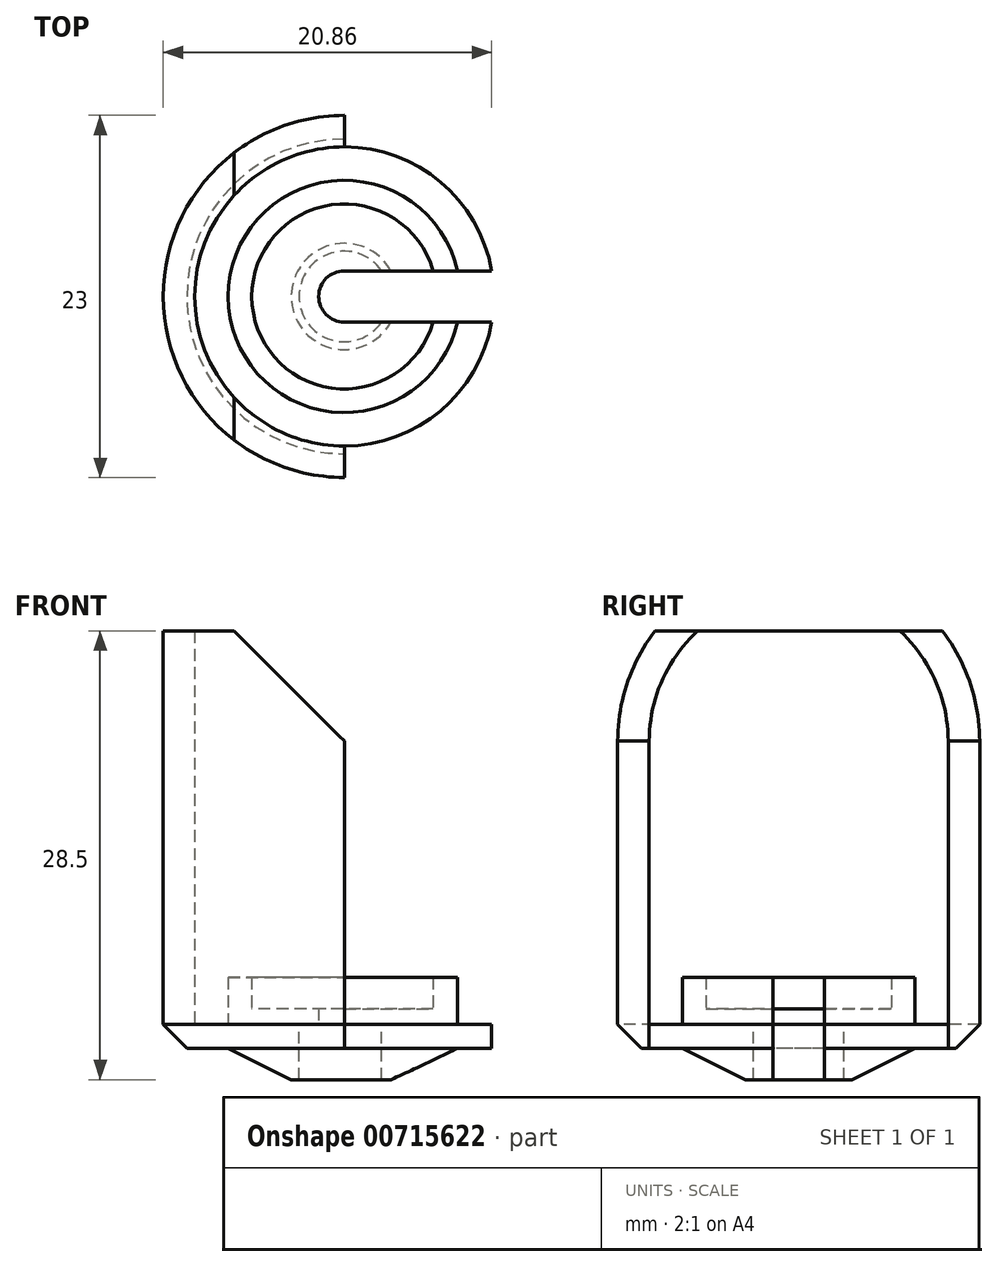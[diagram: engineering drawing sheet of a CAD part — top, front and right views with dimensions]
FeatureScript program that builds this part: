
annotation { "Feature Type Name" : "Feature", "Feature Type Description" : "" }
export const myFeature = defineFeature(function(context is Context, id is Id, definition is map)
    precondition{}
    {
        {
            var Q0;
            Q0=qCreatedBy(makeId("Top.planeOp"),FACE);
            var sketch = newSketch(context, id + "F0", { "sketchPlane" : qUnion([Q0])});
            skArc(sketch, "E0", {"start": v(9.36, 1.63) * mm, "mid": v(-9.5, 0) * mm, "end": v(9.36, -1.62) * mm});
            skArc(sketch, "E1", {"start": v(7.2, 1.62) * mm, "mid": v(-7.38, 0) * mm, "end": v(7.2, -1.63) * mm});
            skArc(sketch, "E2.0", {"start": v(5.65, 1.62) * mm, "mid": v(-5.88, 0) * mm, "end": v(5.65, -1.63) * mm});
            skArc(sketch, "E3", {"start": v(2.37, 1.63) * mm, "mid": v(-2.88, 0) * mm, "end": v(2.37, -1.62) * mm});
            skArc(sketch, "E4", {"start": v(0, 1.63) * mm, "mid": v(-1.63, 0) * mm, "end": v(0, -1.63) * mm});
            skLineSegment(sketch, "E5", {"start": v(0, 1.63) * mm, "end": v(9.36, 1.63) * mm});
            skLineSegment(sketch, "E6", {"start": v(0, -1.63) * mm, "end": v(9.36, -1.63) * mm});
            skArc(sketch, "E7.0", {"start": v(0, 11.5) * mm, "mid": v(-11.5, 0) * mm, "end": v(0, -11.5) * mm});
            skLineSegment(sketch, "E8", {"start": v(0, 9.5) * mm, "end": v(0, 11.5) * mm});
            skLineSegment(sketch, "E9", {"start": v(0, -9.5) * mm, "end": v(0, -11.5) * mm});
            skSolve(sketch);
        }
        {
            var Q0;
            {var subQ0=sQuery(id+"F0.wireOp",EDGE,"E1");Q0=makeQuery(id+"F0.imprint","IMPRINT",FACE,{"disambiguationData":[TD([[makeQuery(id+"F0.imprint","IMPRINT",EDGE,{"derivedFrom":subQ0}),1.0]])]});}
            extrude(context, id + "F1", {"entities" : qUnion([Q0]), "depth" : 3 * mm, "offsetDistance" : 25 * mm});
        }
        {
            var Q0;
            {var subQ0=sQuery(id+"F0.wireOp",EDGE,"E2.0");Q0=makeQuery(id+"F0.imprint","IMPRINT",FACE,{"disambiguationData":[TD([[makeQuery(id+"F0.imprint","IMPRINT",EDGE,{"derivedFrom":subQ0}),1.0]])]});}
            var Q1;
            {var subQ0=sQuery(id+"F0.wireOp",EDGE,"E3");Q1=makeQuery(id+"F0.imprint","IMPRINT",FACE,{"disambiguationData":[TD([[makeQuery(id+"F0.imprint","IMPRINT",EDGE,{"derivedFrom":subQ0}),1.0]])]});}
            extrude(context, id + "F2", {"entities" : qUnion([Q0, Q1]), "operationType" : NewBodyOperationType.ADD, "depth" : 1 * mm, "offsetDistance" : 25 * mm});
        }
        {
            var Q0;
            {var subQ0=sQuery(id+"F0.wireOp",EDGE,"E1");Q0=makeQuery(id+"F0.imprint","IMPRINT",FACE,{"disambiguationData":[TD([[makeQuery(id+"F0.imprint","IMPRINT",EDGE,{"derivedFrom":subQ0}),1.0]])]});}
            var Q1;
            {var subQ0=sQuery(id+"F0.wireOp",EDGE,"E2.0");Q1=makeQuery(id+"F0.imprint","IMPRINT",FACE,{"disambiguationData":[TD([[makeQuery(id+"F0.imprint","IMPRINT",EDGE,{"derivedFrom":subQ0}),1.0]])]});}
            extrude(context, id + "F3", {"entities" : qUnion([Q0, Q1]), "operationType" : NewBodyOperationType.ADD, "oppositeDirection" : true, "depth" : 3.5 * mm, "offsetDistance" : 25 * mm});
        }
        {
            var Q0;
            {var subQ0=sQuery(id+"F0.wireOp",EDGE,"E1");Q0=makeQuery(id+"F0.imprint","IMPRINT",FACE,{"disambiguationData":[TD([[makeQuery(id+"F0.imprint","IMPRINT",EDGE,{"derivedFrom":subQ0}),-1.0]])]});}
            extrude(context, id + "F4", {"entities" : qUnion([Q0]), "operationType" : NewBodyOperationType.ADD, "oppositeDirection" : true, "depth" : 1.5 * mm, "offsetDistance" : 25 * mm});
        }
        {
            var Q0;
            Q0=makeQuery(id+"F0.imprint","IMPRINT",FACE,{"disambiguationData":[TD([[makeQuery(id+"F0.imprint","IMPRINT",EDGE,{"derivedFrom":sQuery(id+"F0.wireOp",EDGE,"E7.0")}),1.0]])]});
            extrude(context, id + "F5", {"entities" : qUnion([Q0]), "operationType" : NewBodyOperationType.ADD, "oppositeDirection" : true, "depth" : 1.5 * mm, "offsetDistance" : 25 * mm});
        }
        {
            var Q0;
            Q0=makeQuery(id+"F0.imprint","IMPRINT",FACE,{"disambiguationData":[TD([[makeQuery(id+"F0.imprint","IMPRINT",EDGE,{"derivedFrom":sQuery(id+"F0.wireOp",EDGE,"E7.0")}),1.0]])]});
            extrude(context, id + "F6", {"entities" : qUnion([Q0]), "operationType" : NewBodyOperationType.ADD, "depth" : 25 * mm, "offsetDistance" : 25 * mm});
        }
        {
            var Q0;
            Q0=makeQuery(id+"F6.opExtrude","CAP_EDGE",EDGE,{"disambiguationData":[OSD([sQuery(id+"F0.wireOp",EDGE,"E9")])],"isStart":false});
            var Q1;
            Q1=makeQuery(id+"F6.opExtrude","CAP_EDGE",EDGE,{"disambiguationData":[OSD([sQuery(id+"F0.wireOp",EDGE,"E8")])],"isStart":false});
            chamfer(context, id + "F7", {"entities" : qUnion([Q0, Q1]), "width" : 7 * mm, "tangentPropagation" : true});
        }
        {
            var Q0;
            Q0=makeQuery(id+"F3.opExtrude","CAP_EDGE",EDGE,{"disambiguationData":[OSD([sQuery(id+"F0.wireOp",EDGE,"E1")])],"isStart":false});
            chamfer(context, id + "F8", {"entities" : qUnion([Q0]), "chamferType" : ChamferType.TWO_OFFSETS, "width1" : 2 * mm, "oppositeDirection" : false, "width2" : 4 * mm, "tangentPropagation" : true});
        }
        {
            var Q0;
            Q0=makeQuery(id+"F5.opExtrude","CAP_EDGE",EDGE,{"disambiguationData":[OSD([sQuery(id+"F0.wireOp",EDGE,"E7.0")])],"isStart":false});
            chamfer(context, id + "F9", {"entities" : qUnion([Q0]), "width" : 1.5 * mm, "tangentPropagation" : true});
        }
    });
